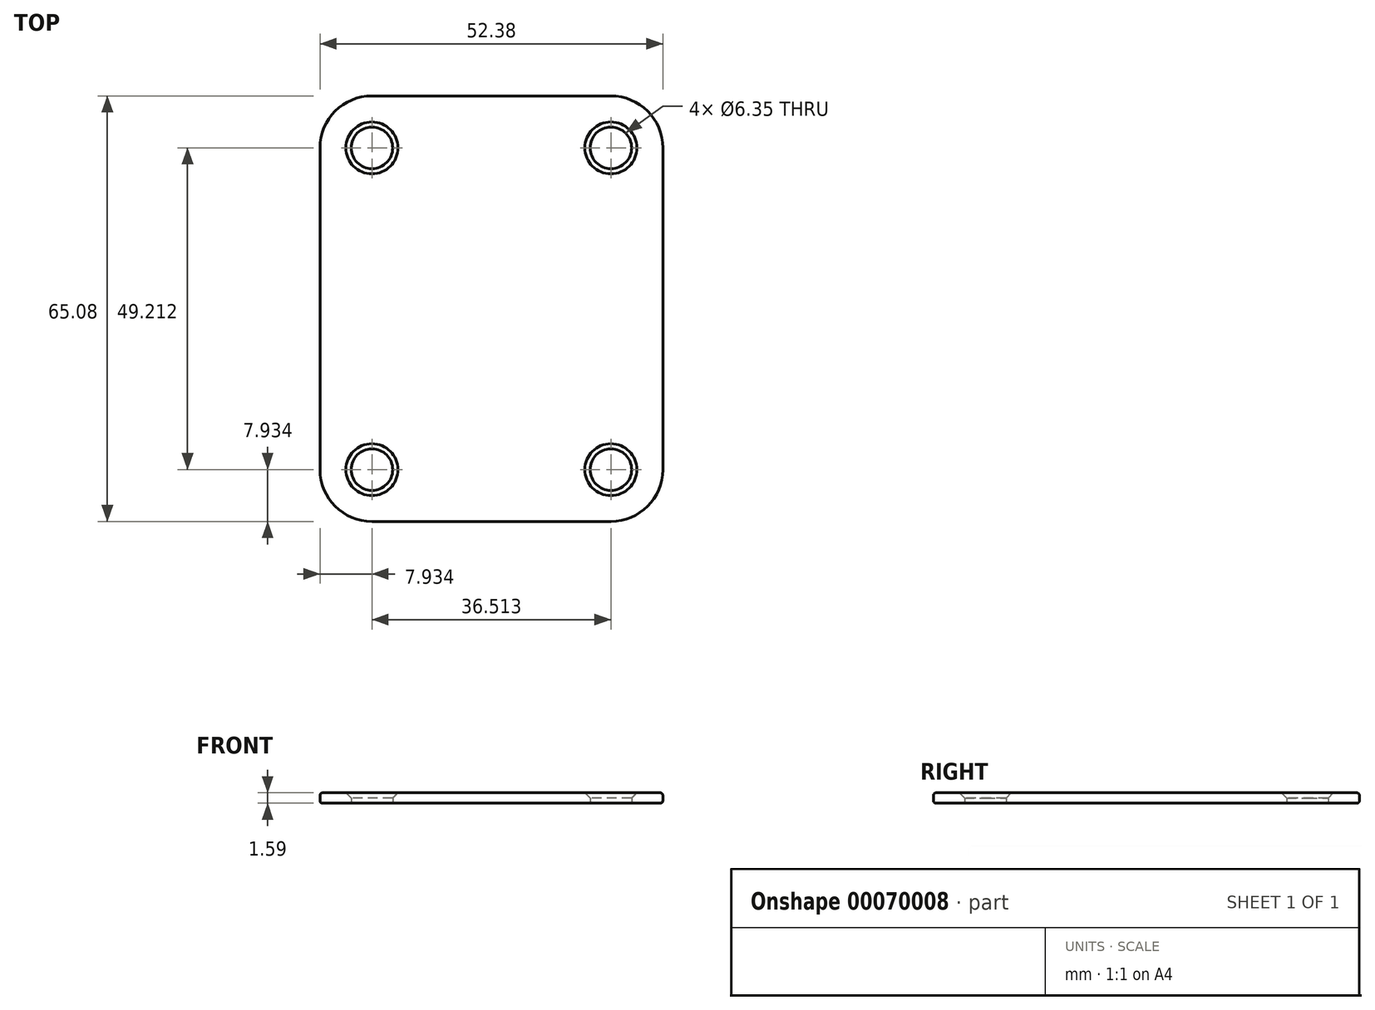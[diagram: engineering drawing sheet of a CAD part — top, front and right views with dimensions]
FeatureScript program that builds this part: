
annotation { "Feature Type Name" : "Feature", "Feature Type Description" : "" }
export const myFeature = defineFeature(function(context is Context, id is Id, definition is map)
    precondition{}
    {
        {
            var Q0;
            Q0=qCreatedBy(makeId("Top.planeOp"),FACE);
            var sketch = newSketch(context, id + "F0", { "sketchPlane" : qUnion([Q0])});
            skLineSegment(sketch, "E0.bottom", {"start": v(-18.26, 32.54) * mm, "end": v(18.26, 32.54) * mm});
            skLineSegment(sketch, "E0.top", {"start": v(-18.26, -32.54) * mm, "end": v(18.26, -32.54) * mm});
            skLineSegment(sketch, "E0.left", {"start": v(-26.2, 24.6) * mm, "end": v(-26.2, -24.6) * mm});
            skLineSegment(sketch, "E0.right", {"start": v(26.2, 24.6) * mm, "end": v(26.2, -24.6) * mm});
            skPoint(sketch, "E0.middle", {"position": v(0, 0) * mm});
            skPoint(sketch, "E1.visualSharp", {"position": v(-26.2, 32.54) * mm});
            skArc(sketch, "E1.filletArc", {"start": v(-18.26, 32.54) * mm, "mid": v(-23.87, 30.22) * mm, "end": v(-26.2, 24.6) * mm});
            skPoint(sketch, "E2.visualSharp", {"position": v(26.2, 32.54) * mm});
            skArc(sketch, "E2.filletArc", {"start": v(26.2, 24.6) * mm, "mid": v(23.87, 30.22) * mm, "end": v(18.26, 32.54) * mm});
            skPoint(sketch, "E3.visualSharp", {"position": v(26.2, -32.54) * mm});
            skArc(sketch, "E3.filletArc", {"start": v(18.26, -32.54) * mm, "mid": v(23.87, -30.22) * mm, "end": v(26.2, -24.6) * mm});
            skPoint(sketch, "E4.visualSharp", {"position": v(-26.2, -32.54) * mm});
            skArc(sketch, "E4.filletArc", {"start": v(-26.2, -24.6) * mm, "mid": v(-23.87, -30.22) * mm, "end": v(-18.26, -32.54) * mm});
            skCircle(sketch, "E5", {"center": v(18.26, 24.6) * mm, "radius": 3.18 * mm});
            skCircle(sketch, "E6", {"center": v(18.26, -24.6) * mm, "radius": 3.18 * mm});
            skCircle(sketch, "E7", {"center": v(-18.26, -24.6) * mm, "radius": 3.18 * mm});
            skCircle(sketch, "E8", {"center": v(-18.26, 24.6) * mm, "radius": 3.18 * mm});
            skSolve(sketch);
        }
        {
            var Q0;
            Q0 = qSketchRegion(id + "F0", true);
            extrude(context, id + "F1", {"entities" : qUnion([Q0]), "depth" : 1.59 * mm});
        }
        {
            var Q0;
            Q0=makeQuery(id+"F1.opExtrude","SWEPT_FACE",FACE,{"disambiguationData":[OSD([sQuery(id+"F0.wireOp",EDGE,"E0.top")])]});
            var Q1;
            Q1=makeQuery(id+"F1.opExtrude","SWEPT_FACE",FACE,{"disambiguationData":[OSD([sQuery(id+"F0.wireOp",EDGE,"E3.filletArc")])]});
            var Q2;
            Q2=makeQuery(id+"F1.opExtrude","SWEPT_FACE",FACE,{"disambiguationData":[OSD([sQuery(id+"F0.wireOp",EDGE,"E0.right")])]});
            var Q3;
            Q3=makeQuery(id+"F1.opExtrude","SWEPT_FACE",FACE,{"disambiguationData":[OSD([sQuery(id+"F0.wireOp",EDGE,"E4.filletArc")])]});
            var Q4;
            Q4=makeQuery(id+"F1.opExtrude","SWEPT_FACE",FACE,{"disambiguationData":[OSD([sQuery(id+"F0.wireOp",EDGE,"E0.left")])]});
            var Q5;
            Q5=makeQuery(id+"F1.opExtrude","SWEPT_FACE",FACE,{"disambiguationData":[OSD([sQuery(id+"F0.wireOp",EDGE,"E1.filletArc")])]});
            var Q6;
            Q6=makeQuery(id+"F1.opExtrude","SWEPT_FACE",FACE,{"disambiguationData":[OSD([sQuery(id+"F0.wireOp",EDGE,"E0.bottom")])]});
            var Q7;
            Q7=makeQuery(id+"F1.opExtrude","SWEPT_FACE",FACE,{"disambiguationData":[OSD([sQuery(id+"F0.wireOp",EDGE,"E2.filletArc")])]});
            fillet(context, id + "F2", {"entities" : qUnion([Q0, Q1, Q2, Q3, Q4, Q5, Q6, Q7]), "radius" : 0.4 * mm, "tangentPropagation" : true, "allowEdgeOverflow" : false});
        }
        {
            var Q0;
            Q0=makeQuery(id+"F1.opExtrude","CAP_EDGE",EDGE,{"disambiguationData":[OSD([sQuery(id+"F0.wireOp",EDGE,"E6")])],"isStart":false});
            var Q1;
            Q1=makeQuery(id+"F1.opExtrude","CAP_EDGE",EDGE,{"disambiguationData":[OSD([sQuery(id+"F0.wireOp",EDGE,"E7")])],"isStart":false});
            var Q2;
            Q2=makeQuery(id+"F1.opExtrude","CAP_EDGE",EDGE,{"disambiguationData":[OSD([sQuery(id+"F0.wireOp",EDGE,"E8")])],"isStart":false});
            var Q3;
            Q3=makeQuery(id+"F1.opExtrude","CAP_EDGE",EDGE,{"disambiguationData":[OSD([sQuery(id+"F0.wireOp",EDGE,"E5")])],"isStart":false});
            chamfer(context, id + "F3", {"entities" : qUnion([Q0, Q1, Q2, Q3]), "width" : 0.8 * mm, "tangentPropagation" : true});
        }
    });
